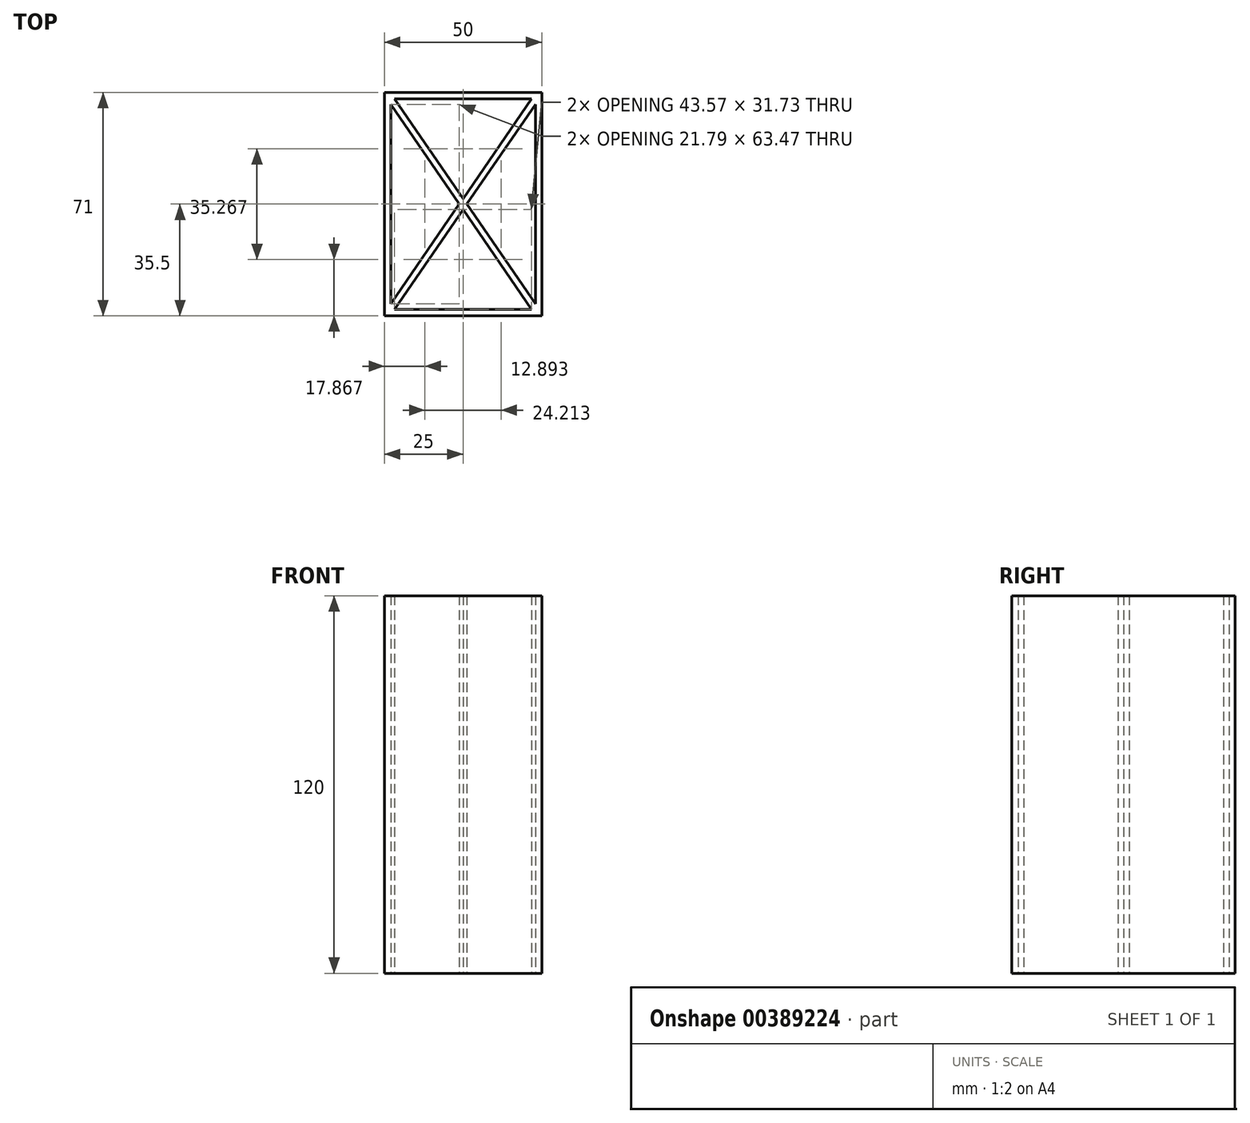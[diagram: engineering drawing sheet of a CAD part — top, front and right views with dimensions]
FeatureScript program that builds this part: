
annotation { "Feature Type Name" : "Feature", "Feature Type Description" : "" }
export const myFeature = defineFeature(function(context is Context, id is Id, definition is map)
    precondition{}
    {
        {
            var Q0;
            Q0=qCreatedBy(makeId("Top.planeOp"),FACE);
            var sketch = newSketch(context, id + "F0", { "sketchPlane" : qUnion([Q0])});
            skLineSegment(sketch, "E0.bottom", {"start": v(0, 0) * mm, "end": v(50, 0) * mm});
            skLineSegment(sketch, "E0.top", {"start": v(0, 71) * mm, "end": v(50, 71) * mm});
            skLineSegment(sketch, "E0.left", {"start": v(0, 0) * mm, "end": v(0, 71) * mm});
            skLineSegment(sketch, "E0.right", {"start": v(50, 0) * mm, "end": v(50, 71) * mm});
            skLineSegment(sketch, "E1.bottom", {"start": v(3.21, 2) * mm, "end": v(46.79, 2) * mm});
            skLineSegment(sketch, "E1.top", {"start": v(3.21, 69) * mm, "end": v(46.79, 69) * mm});
            skLineSegment(sketch, "E1.left", {"start": v(2, 3.77) * mm, "end": v(2, 67.23) * mm});
            skLineSegment(sketch, "E1.right", {"start": v(48, 3.77) * mm, "end": v(48, 67.23) * mm});
            skLineSegment(sketch, "E2", {"start": v(3.21, 2) * mm, "end": v(25, 33.73) * mm});
            skLineSegment(sketch, "E3", {"start": v(46.79, 69) * mm, "end": v(25, 37.27) * mm});
            skLineSegment(sketch, "E4", {"start": v(2, 67.23) * mm, "end": v(23.79, 35.5) * mm});
            skLineSegment(sketch, "E5", {"start": v(3.21, 69) * mm, "end": v(25, 37.27) * mm});
            skLineSegment(sketch, "E6", {"start": v(48, 69) * mm, "end": v(2, 2) * mm, "construction": true});
            skLineSegment(sketch, "E7", {"start": v(2, 69) * mm, "end": v(48, 2) * mm, "construction": true});
            skLineSegment(sketch, "E8.trimOffspring", {"start": v(25, 33.73) * mm, "end": v(46.79, 2) * mm});
            skLineSegment(sketch, "E9.trimOffspring", {"start": v(26.21, 35.5) * mm, "end": v(48, 67.23) * mm});
            skLineSegment(sketch, "E10.trimOffspring", {"start": v(26.21, 35.5) * mm, "end": v(48, 3.77) * mm});
            skLineSegment(sketch, "E11.trimOffspring", {"start": v(23.79, 35.5) * mm, "end": v(2, 3.77) * mm});
            skSolve(sketch);
        }
        {
            var Q0;
            Q0 = qSketchRegion(id + "F0", true);
            extrude(context, id + "F1", {"entities" : qUnion([Q0]), "depth" : 120 * mm});
        }
    });
